# Revit family: Duct_Accessory_In-O-Vate_6WV-Wall-Vent
name_source: partatom
category: Duct Accessories
units: mm (PartAtom-declared; Revit-internal decimal feet)

## family parameters
Cut with Voids When Loaded = No
Host = Face
OmniClass Number = 23.75.70.14.34
OmniClass Title = Air Duct Accessories
Part Type = Attaches To
Round Connector Dimension = Use Diameter
Shared = No

## types (5) — shared parameters
Default Elevation = 48 "
Depth = 2.34 "
Height = 8.51 "
Manufacturer = InOvate Technologies Inc.
Product Documentation Link = https://premiumwallvent.com
Product Page URL = https://premiumwallvent.com
Product data url = https://www.bimobject.com
URL = https://inovate.com
Width = 8.51 "

## per-type parameters (varying)
| type | Color | Description | Model | Product Material |
| 6WVW - White | White | Low-Profile Vent Closure for Additional Application, White | 6WVW | InOvate-Metal-White |
| 6WVT - Tan | Tan | Low-Profile Vent Closure for Additional Application, Tan | 6WVT | InOvate-Metal-Tan |
| 6WVB - Brown | Brown | Low-Profile Vent Closure for Additional Application, Brown | 6WVB | InOvate-Metal-Brown |
| 6WVK - Black | Black | Low-Profile Vent Closure for Additional Application, Black | 6WVK | InOvate-Metal-Black |
| 6WVP - Primer | Primer | Low-Profile Vent Closure for Additional Application, Primer | 6WVP | InOvate-Metal-Primer |

## geometry (parser evidence)
native form markers: Sweep x5
no freeform markers — native parametric forms only
